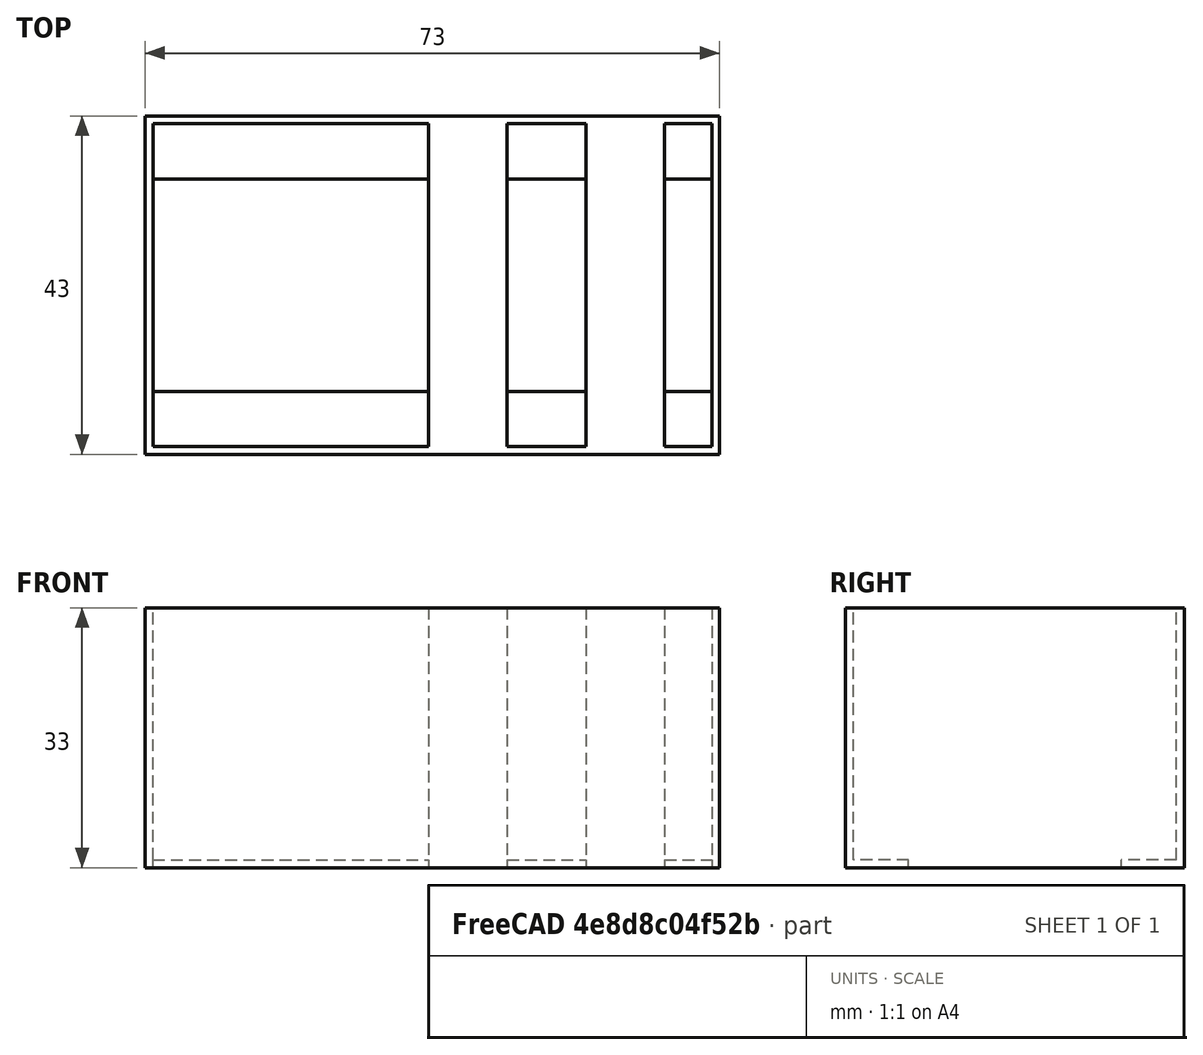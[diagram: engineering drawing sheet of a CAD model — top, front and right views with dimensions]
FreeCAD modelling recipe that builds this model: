
FCSTD DOCUMENT  (FreeCAD 0.18R4 (GitTag))
Label: woodland
License: All rights reserved
LicenseURL: http://en.wikipedia.org/wiki/All_rights_reserved
objects: Part::Box×8, Part::Cut×2, Part::MultiFuse×2
note: 12 computed .brp shape members not serialized (recipe doc carries the construction recipe); baked Part::Feature solids carry a one-line shape summary decoded from their .brp

FEATURE [Part::Box] Box  label="Cube"
  AttacherType = Attacher::AttachEngine3D
  Height = 33
  Length = 202
  Width = 43
FEATURE [Part::Box] Box001  label="Cube001"
  AttacherType = Attacher::AttachEngine3D
  Height = 33
  Length = 200
  Placement = pos=(1,1,0) rot=(0,0,1;0rad)
  Width = 41
FEATURE [Part::Cut] Cut
  Base = -> Box
  Tool = -> Box001
FEATURE [Part::Box] Box002  label="Cube002"
  AttacherType = Attacher::AttachEngine3D
  Height = 1
  Length = 202
  Width = 8
FEATURE [Part::Box] Box003  label="Cube003"
  AttacherType = Attacher::AttachEngine3D
  Height = 1
  Length = 202
  Placement = pos=(0,35,0) rot=(0,0,1;0rad)
  Width = 8
FEATURE [Part::MultiFuse] Fusion
  Shapes = -> [Cut,Box002,Box003]
FEATURE [Part::Box] Box004  label="Cube004"
  AttacherType = Attacher::AttachEngine3D
  Height = 33
  Length = 10
  Placement = pos=(36,0,0) rot=(0,0,1;0rad)
  Width = 43
FEATURE [Part::Box] Box005  label="Cube005"
  AttacherType = Attacher::AttachEngine3D
  Height = 33
  Length = 10
  Placement = pos=(56,0,0) rot=(0,0,1;0rad)
  Width = 43
FEATURE [Part::Box] Box006  label="Cube006"
  AttacherType = Attacher::AttachEngine3D
  Height = 33
  Length = 10
  Placement = pos=(72,0,0) rot=(0,0,1;0rad)
  Width = 43
FEATURE [Part::Box] Box007  label="Cube007"
  AttacherType = Attacher::AttachEngine3D
  Height = 33
  Length = 129
  Placement = pos=(73,0,0) rot=(0,0,1;0rad)
  Width = 43
FEATURE [Part::MultiFuse] Fusion001
  Shapes = -> [Fusion,Box004,Box005,Box006]
FEATURE [Part::Cut] Cut001
  Base = -> Fusion001
  Tool = -> Box007
